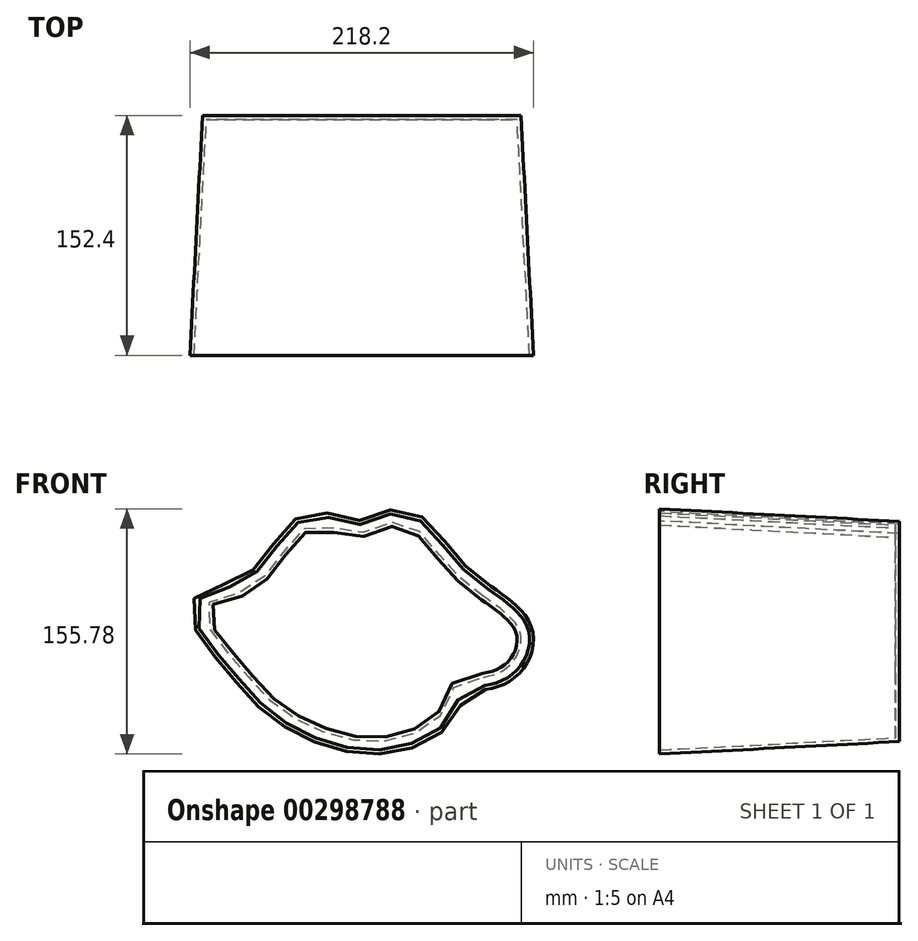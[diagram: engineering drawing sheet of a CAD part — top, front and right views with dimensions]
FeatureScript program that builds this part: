
annotation { "Feature Type Name" : "Feature", "Feature Type Description" : "" }
export const myFeature = defineFeature(function(context is Context, id is Id, definition is map)
    precondition{}
    {
        {
            var Q0;
            Q0=qCreatedBy(makeId("Front.planeOp"),FACE);
            var sketch = newSketch(context, id + "F0", { "sketchPlane" : qUnion([Q0])});
            skLineSegment(sketch, "E0.right", {"start": v(85.87, 44.68) * mm, "end": v(85.87, 41.35) * mm});
            skPoint(sketch, "E1.visualSharp", {"position": v(-66.53, 70.08) * mm});
            skPoint(sketch, "E2.visualSharp", {"position": v(-66.53, -31.52) * mm});
            skPoint(sketch, "E3.visualSharp", {"position": v(85.87, -31.52) * mm});
            skArc(sketch, "E3.filletArc", {"start": v(85.6, -9.82) * mm, "mid": v(85.8, -7.97) * mm, "end": v(85.87, -6.12) * mm});
            skPoint(sketch, "E4.visualSharp", {"position": v(85.87, 70.08) * mm});
            skFitSpline(sketch, "E5", {"points": [v(-41.13, 70.08) * mm, v(-66.53, 44.68) * mm, v(-92.46, 33.78) * mm, v(-66.53, -6.12) * mm, v(-41.13, -31.52) * mm, v(17.11, -50.67) * mm, v(60.47, -31.52) * mm, v(68.9, -14.22) * mm, v(97.12, -6.12) * mm, v(108.68, 19.34) * mm, v(70.23, 53.78) * mm, v(34.8, 88.9) * mm, v(5.27, 81.44) * mm, v(-21.33, 87.28) * mm, v(-41.13, 70.08) * mm]});
            skSolve(sketch);
        }
        {
            var Q0;
            {var subQ0=sQuery(id+"F0.wireOp",EDGE,"E5");var subQ1=makeQuery(id+"F0.imprint","IMPRINT",VERTEX,{"disambiguationData":[OD(0.0)],"derivedFrom":subQ0});Q0=makeQuery(id+"F0.imprint","IMPRINT",FACE,{"disambiguationData":[TD([[makeQuery(id+"F0.imprint","IMPRINT",EDGE,{"disambiguationData":[TD([[subQ1,1.0]])],"derivedFrom":subQ0}),1.0]])]});}
            extrude(context, id + "F1", {"entities" : qUnion([Q0]), "depth" : 152.4 * mm, "hasDraft" : true, "draftAngle" : 3 * degree});
        }
        {
            var Q0;
            Q0=makeQuery(id+"F1.opExtrude","CAP_FACE",FACE,{"disambiguationData":[OSD([sQuery(id+"F0.wireOp",EDGE,"E5")])],"isStart":false});
            shell(context, id + "F2", {"entities" : qUnion([Q0]), "thickness" : 2.54 * mm});
        }
    });
